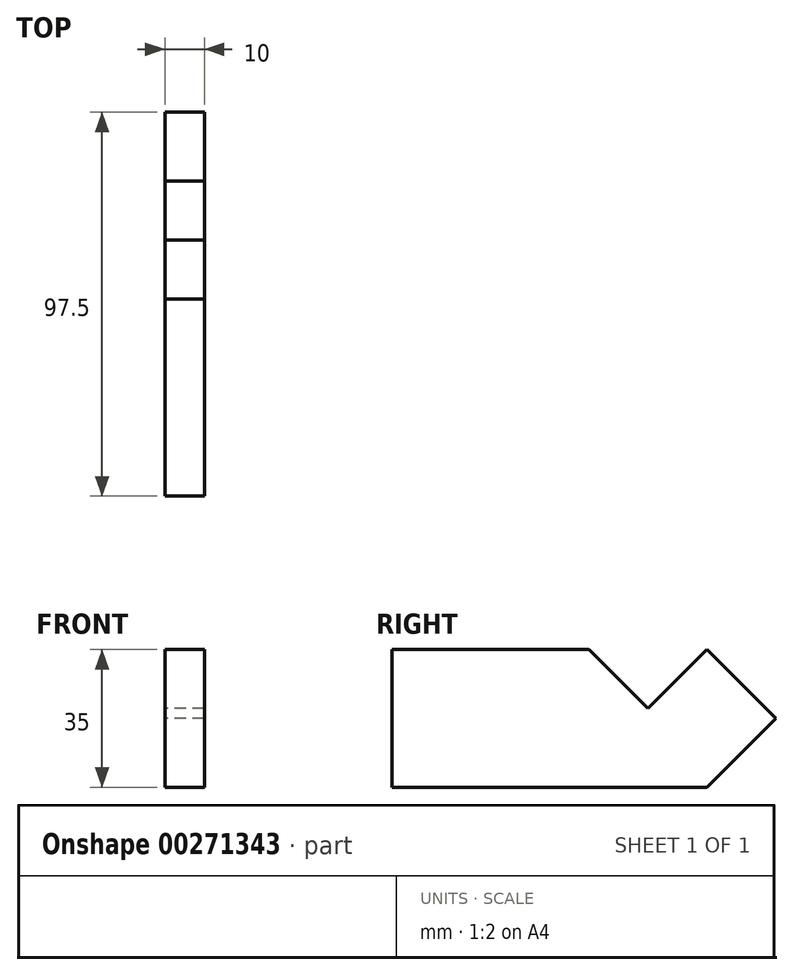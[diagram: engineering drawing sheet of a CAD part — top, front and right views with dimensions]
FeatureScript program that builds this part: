
annotation { "Feature Type Name" : "Feature", "Feature Type Description" : "" }
export const myFeature = defineFeature(function(context is Context, id is Id, definition is map)
    precondition{}
    {
        {
            var Q0;
            Q0=qCreatedBy(makeId("Right.planeOp"),FACE);
            var sketch = newSketch(context, id + "F0", { "sketchPlane" : qUnion([Q0])});
            skLineSegment(sketch, "E0", {"start": v(0, 0) * mm, "end": v(0, 35) * mm});
            skLineSegment(sketch, "E1", {"start": v(0, 0) * mm, "end": v(80, 0) * mm});
            skLineSegment(sketch, "E2", {"start": v(0, 35) * mm, "end": v(50, 35) * mm});
            skLineSegment(sketch, "E3", {"start": v(65, 20) * mm, "end": v(50, 35) * mm});
            skLineSegment(sketch, "E4", {"start": v(80, 35) * mm, "end": v(65, 20) * mm});
            skLineSegment(sketch, "E5", {"start": v(97.5, 17.5) * mm, "end": v(80, 35) * mm});
            skLineSegment(sketch, "E6", {"start": v(80, 0) * mm, "end": v(97.5, 17.5) * mm});
            skSolve(sketch);
        }
        {
            var Q0;
            Q0=makeQuery(id+"F0.imprint","IMPRINT",FACE,{"disambiguationData":[TD([[makeQuery(id+"F0.imprint","IMPRINT",EDGE,{"derivedFrom":sQuery(id+"F0.wireOp",EDGE,"E0")}),-1.0]])]});
            extrude(context, id + "F1", {"entities" : qUnion([Q0]), "depth" : 10 * mm});
        }
    });
